# Revit family: Hand_Hair_Dryer-Automatic-American_Dryer-Advantage
name_source: partatom
category: Specialty Equipment
revit_build: Autodesk Revit 2015 (Build: 20140606_1530(x64)
units: mm (PartAtom-declared; Revit-internal decimal feet)

## types (30) — shared parameters
Accessory Material = Metal - American Dryer - Stainless Steel #4 brush
Amperage = 0 A
Amperage Range = 6.5 - 12.5 A
Assembly Code = C1030200
BIMobject category = Dryers (Hand & Hair)
BIMobject category code = sanitary-hand-and-hair-dryers
BIMobject main category = Sanitary
BIMobject main category code = sanitary
Brand url = http://worlddryer.com
Connector Descriptor = Power Connection
Default Elevation = 4' - 0"
Design country = United States
Edition number = 1
Installation instructions = https://www.americandryer.com
Load Classification = Other
Load Sub Classification Motor = No
Manufacturer = American Dryer
Manufacturer Fax = 734.421.5580
Manufacturer country = United States
Manufacturer name = World Dryer
Material main = Steel
Nominal height = 0' - 0"
Nominal width = 0' - 0"
Number of Poles = 1
OmniClass Code = 23-31 25 15
OmniClass Description = Hand Dryers
Product Documentation Link = http://www.americandryer.com
Product Guid = 5c203d2d-28f6-4a6b-afd4-88badfebff29
Product Page URL = http://www.americandryer.com
Product SKU = hand-dryer-world-dryer-advantage-series
Product certification = https://www.americandryer.com
Product data url = https://bimobject.com
Product family = Hand and Hair Dryers
Product group = Advantage Series
Product url = http://www.americandryer.com
QR code = http://bimobject.com
Series = Advantage
Technical description = https://www.americandryer.com
URL = http://www.americandryer.com
Uniclass 2.0 Code = PR-02-03
Uniclass 2.0 Description = Air Dryers
Uniclass 2015 Code = Pr_40_20_76
Uniclass 2015 Name = Sanitary accessories
Version = 1
Voltage = 0 V
Voltage Range = 100 - 240 V
Watts = 0 W
Weight Net (Kg) = 0
zero-valued in all types: Power Factor

## per-type parameters (varying)
| type | ADA Compliant | Case Material | Description | Overall Depth | Overall Height | Overall Width | Shipping Weight | With ADA Recess Kit | With ADA Wall Guard | With Adapter Plate |
| AD90 | No | Plastic - American Dryer - ABS Retardant White | Hand Dryer | 0' - 5 5/8" | 0' - 9 1/16" | 0' - 9 13/16" | 9.00 lb | No | No | No |
| AD90-M | No | Metal - American Dryer - Steel White Epoxy | Hand Dryer | 0' - 5 5/8" | 0' - 9 1/16" | 0' - 9 13/16" | 10.00 lb | No | No | No |
| AD90-BG | No | Metal - American Dryer - Steel Black Graphite Epoxy | Hand Dryer | 0' - 5 5/8" | 0' - 9 1/16" | 0' - 9 13/16" | 10.00 lb | No | No | No |
| AD90-C | No | Metal - American Dryer - Steel Chrome | Hand Dryer | 0' - 5 5/8" | 0' - 9 1/16" | 0' - 9 13/16" | 10.00 lb | No | No | No |
| AD90-SS | No | Metal - American Dryer - Stainless Steel #4 brush | Hand Dryer | 0' - 5 5/8" | 0' - 9 1/16" | 0' - 9 13/16" | 10.00 lb | No | No | No |
| AD90(AP) | No | Plastic - American Dryer - ABS Retardant White | Hand Dryer | 0' - 5 11/16" | 1' - 2" | 1' - 4" | 14.00 lb | No | No | Yes |
| AD90-M(AP) | No | Metal - American Dryer - Steel White Epoxy | Hand Dryer | 0' - 5 11/16" | 1' - 2" | 1' - 4" | 15.00 lb | No | No | Yes |
| AD90-BG(AP) | No | Metal - American Dryer - Steel Black Graphite Epoxy | Hand Dryer | 0' - 5 11/16" | 1' - 2" | 1' - 4" | 15.00 lb | No | No | Yes |
| AD90-C(AP) | No | Metal - American Dryer - Steel Chrome | Hand Dryer | 0' - 5 11/16" | 1' - 2" | 1' - 4" | 15.00 lb | No | No | Yes |
| AD90-SS(AP) | No | Metal - American Dryer - Stainless Steel #4 brush | Hand Dryer | 0' - 5 11/16" | 1' - 2" | 1' - 4" | 15.00 lb | No | No | Yes |
| AD90(WG) | Yes | Plastic - American Dryer - ABS Retardant White | Hand Dryer | 0' - 5 5/8" | 2' - 3 23/32" | 0' - 9 13/16" | 12.00 lb | No | Yes | No |
| AD90-M(WG) | Yes | Metal - American Dryer - Steel White Epoxy | Hand Dryer | 0' - 5 5/8" | 2' - 3 23/32" | 0' - 9 13/16" | 14.00 lb | No | Yes | No |
| AD90-BG(WG) | Yes | Metal - American Dryer - Steel Black Graphite Epoxy | Hand Dryer | 0' - 5 5/8" | 2' - 3 23/32" | 0' - 9 13/16" | 14.00 lb | No | Yes | No |
| AD90-C(WG) | Yes | Metal - American Dryer - Steel Chrome | Hand Dryer | 0' - 5 5/8" | 2' - 3 23/32" | 0' - 9 13/16" | 14.00 lb | No | Yes | No |
| AD90-SS(WG) | Yes | Metal - American Dryer - Stainless Steel #4 brush | Hand Dryer | 0' - 5 5/8" | 2' - 3 23/32" | 0' - 9 13/16" | 14.00 lb | No | Yes | No |
| AD90(RK) | Yes | Plastic - American Dryer - ABS Retardant White | Hand Dryer | 0' - 5 11/16" | 1' - 9 1/4" | 1' - 4 1/4" | 15.00 lb | Yes | No | No |
| AD90-M(RK) | Yes | Metal - American Dryer - Steel White Epoxy | Hand Dryer | 0' - 5 11/16" | 1' - 9 1/4" | 1' - 4 1/4" | 17.00 lb | Yes | No | No |
| AD90-BG(RK) | Yes | Metal - American Dryer - Steel Black Graphite Epoxy | Hand Dryer | 0' - 5 11/16" | 1' - 9 1/4" | 1' - 4 1/4" | 17.00 lb | Yes | No | No |
| AD90-C(RK) | Yes | Metal - American Dryer - Steel Chrome | Hand Dryer | 0' - 5 11/16" | 1' - 9 1/4" | 1' - 4 1/4" | 17.00 lb | Yes | No | No |
| AD90-SS(RK) | Yes | Metal - American Dryer - Stainless Steel #4 brush | Hand Dryer | 0' - 5 11/16" | 1' - 9 1/4" | 1' - 4 1/4" | 17.00 lb | Yes | No | No |
| AD90(H) | No | Plastic - American Dryer - ABS Retardant White | Hair Dryer | 0' - 5 5/8" | 0' - 9 1/16" | 0' - 9 13/16" | 9.00 lb | No | No | No |
| AD90-M(H) | No | Metal - American Dryer - Steel White Epoxy | Hair Dryer | 0' - 5 5/8" | 0' - 9 1/16" | 0' - 9 13/16" | 10.00 lb | No | No | No |
| AD90-BG(H) | No | Metal - American Dryer - Steel Black Graphite Epoxy | Hair Dryer | 0' - 5 5/8" | 0' - 9 1/16" | 0' - 9 13/16" | 10.00 lb | No | No | No |
| AD90-C(H) | No | Metal - American Dryer - Steel Chrome | Hair Dryer | 0' - 5 5/8" | 0' - 9 1/16" | 0' - 9 13/16" | 10.00 lb | No | No | No |
| AD90-SS(H) | No | Metal - American Dryer - Stainless Steel #4 brush | Hair Dryer | 0' - 5 5/8" | 0' - 9 1/16" | 0' - 9 13/16" | 10.00 lb | No | No | No |
| AD90(H)(AP) | No | Plastic - American Dryer - ABS Retardant White | Hair Dryer | 0' - 5 11/16" | 1' - 2" | 1' - 4" | 14.00 lb | No | No | Yes |
| AD90-M(H)(AP) | No | Metal - American Dryer - Steel White Epoxy | Hair Dryer | 0' - 5 11/16" | 1' - 2" | 1' - 4" | 15.00 lb | No | No | Yes |
| AD90-BG(H)(AP) | No | Metal - American Dryer - Steel Black Graphite Epoxy | Hair Dryer | 0' - 5 11/16" | 1' - 2" | 1' - 4" | 15.00 lb | No | No | Yes |
| AD90-C(H)(AP) | No | Metal - American Dryer - Steel Chrome | Hair Dryer | 0' - 5 11/16" | 1' - 2" | 1' - 4" | 15.00 lb | No | No | Yes |
| AD90-SS(H)(AP) | No | Metal - American Dryer - Stainless Steel #4 brush | Hair Dryer | 0' - 5 11/16" | 1' - 2" | 1' - 4" | 15.00 lb | No | No | Yes |

note: column(s) folded — value = type name in every type: Model

## geometry (parser evidence)
native form markers: Sweep x2
no freeform markers — native parametric forms only
